# Revit family: Washer_Milnor_60lb-Capacity_30022T6X
name_source: partatom
category: Mechanical Equipment
units: mm (PartAtom-declared; Revit-internal decimal feet)

## family parameters
Always vertical = No
Cut with Voids When Loaded = No
Maintain Annotation Orientation = No
OmniClass Number = 23.45.70.11.14.11
OmniClass Title = Washing Machines
Part Type = Normal
Room Calculation Point = No
Round Connector Dimension = Use Diameter
Shared = No
Work Plane-Based = Yes

## types (1)
- 3022T6XBE2015252D
    16" Clearance = Yes
    Assembly Code = E1010610
    Capacity = 60 lb
    Construction Details = https://www.arcat.com
    Cylinder Depth = 1' - 3"
    Cylinder Diameter = 2' - 6"
    Cylinder Volume = 9 CF
    Default Elevation = 4' - 0"
    Description = Milnor Commercial Washer Extractor
    Door Base from FF = 2' - 1"
    Door Opening = 1' - 3 1/2"
    Door Opening Depth = 1' - 3 3/4"
    Dynamic Load = 0.00 kip
    Expected Lifespan (Years) = 12
    Extraction G-Force = 140 Gs
    Frequency = 60 Hz
    Green Building-LEED = https://www.arcat.com
    Installation-Fabrication = https://www.arcat.com
    Keynote = 11110
    MEP Amperage = 19 A
    Maintenance Schedule (Months) = 0
    Manufacturer = Pellerin Milnor Corp
    Manufacturer Fax = 504-468-3094
    Manufacturer Website = http://www.milnor.com
    Model = 3022T6XBE2015252D
    Number of Poles = 1
    Phase = 3
    Product Data = http://www.arcat.com
    Product Properties = https://www.arcat.com
    Revision = R1_08-2018
    Sales Information = http://www.milnor.com
    Send Message = http://www.arcat.com
    SpecWizard = https://www.arcat.com
    Specification = https://www.arcat.com
    Suspension Type = Rigid
    URL = http://www.milnor.com
    Unit Depth = 3' - 9 3/4"
    Unit Height = 4' - 6"
    Unit Weight = 944
    Unit Width = 2' - 10 1/2"
    Vibration Frequency = 0
    Voltage_MEP = 45 V
    Warranty Duration (Years) = 5
    doorgas = 1' - 6"

## geometry (parser evidence)
native form markers: Sweep x3
no freeform markers — native parametric forms only
